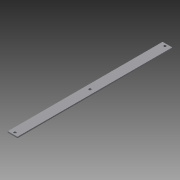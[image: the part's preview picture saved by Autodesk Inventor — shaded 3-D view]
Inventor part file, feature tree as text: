
AUTODESK INVENTOR PART (.ipt)
format: ipt  version: 2015 (Build 190159000, 159)  size: 81,920 bytes
history: native  units: in
note: dims shown in document units (in); Inventor stores cm internally (conversion verified against a paired STEP export)
features: sketch x2, extrude x1, hole x1
ambient origin geometry x8: Origin, YZ Plane, XZ Plane, XY Plane, X Axis, Y Axis, Z Axis, Center Point
bodies: Solid1 (feature_tree)
feature tree (4):
  extrude  "Extrusion1"  Depth=0.125in
  hole  "Hole1"  [1 undecoded]
  sketch  "Sketch1"  dims[d0=1.0in d1=0.125in]
  sketch  "Sketch2"  dims[d2=16.0in d3=0.0in d4=0.25in d5=0.25in d6=8.0in d7=0.25in d8=0.75in d9=0.375in d10=0.25in d11=0.5635in d12=1.0in d13=0.8108in]
note: 1 required parameter value undecoded (feature->parameter linkage not recoverable at this tier; creation-order binding heuristic only, values carry confidence <= 0.55)
